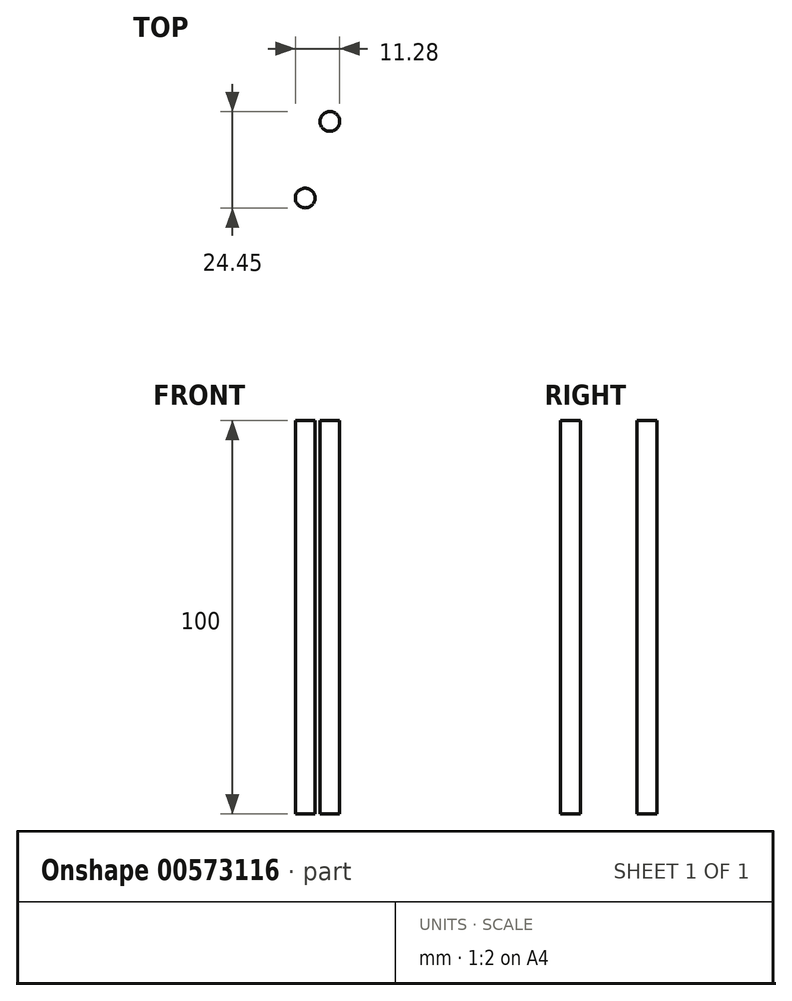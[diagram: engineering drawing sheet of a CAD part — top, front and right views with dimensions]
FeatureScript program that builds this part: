
annotation { "Feature Type Name" : "Feature", "Feature Type Description" : "" }
export const myFeature = defineFeature(function(context is Context, id is Id, definition is map)
    precondition{}
    {
        {
            var Q0;
            Q0=qCreatedBy(makeId("Top.planeOp"),FACE);
            var sketch = newSketch(context, id + "F0", { "sketchPlane" : qUnion([Q0])});
            skCircle(sketch, "E0", {"center": v(-44.2, -60.28) * mm, "radius": 2.5 * mm});
            skCircle(sketch, "E1", {"center": v(-37.92, -40.83) * mm, "radius": 2.5 * mm});
            skSolve(sketch);
        }
        {
            var Q0;
            Q0=makeQuery(id+"F0.imprint","IMPRINT",FACE,{"disambiguationData":[TD([[makeQuery(id+"F0.imprint","IMPRINT",EDGE,{"derivedFrom":sQuery(id+"F0.wireOp",EDGE,"E0")}),1.0]])]});
            var Q1;
            Q1=makeQuery(id+"F0.imprint","IMPRINT",FACE,{"disambiguationData":[TD([[makeQuery(id+"F0.imprint","IMPRINT",EDGE,{"derivedFrom":sQuery(id+"F0.wireOp",EDGE,"E1")}),1.0]])]});
            extrude(context, id + "F1", {"entities" : qUnion([Q0, Q1]), "depth" : 100 * mm, "offsetDistance" : 25.4 * mm});
        }
    });
